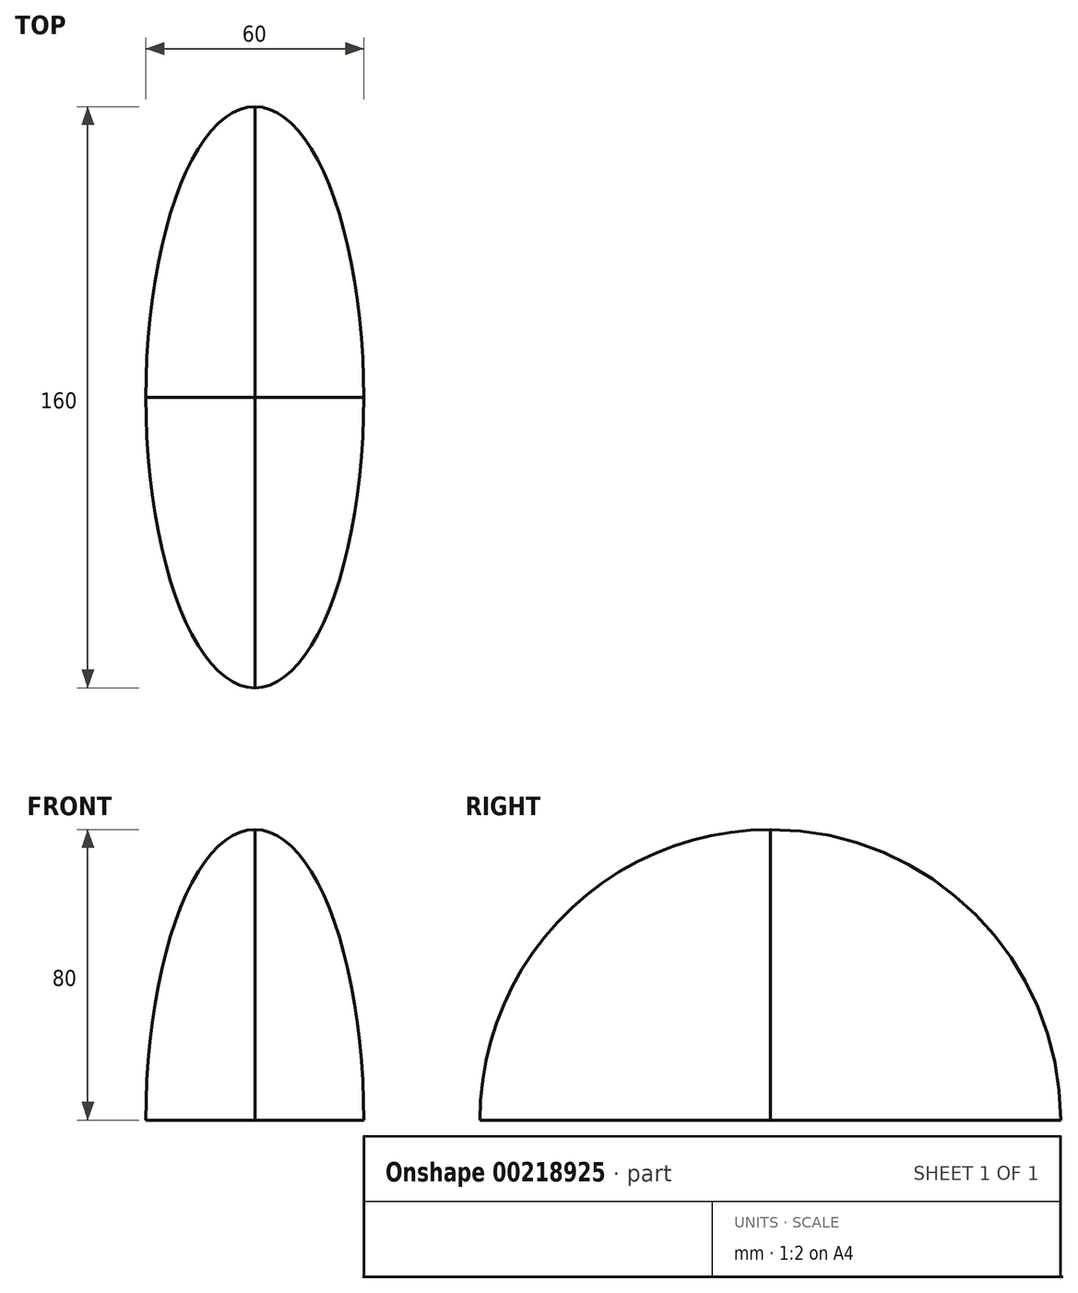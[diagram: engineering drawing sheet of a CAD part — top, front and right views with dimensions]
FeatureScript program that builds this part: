
annotation { "Feature Type Name" : "Feature", "Feature Type Description" : "" }
export const myFeature = defineFeature(function(context is Context, id is Id, definition is map)
    precondition{}
    {
        {
            var Q0;
            Q0=qCreatedBy(makeId("Top.planeOp"),FACE);
            var sketch = newSketch(context, id + "F0", { "sketchPlane" : qUnion([Q0])});
            skEllipticalArc(sketch, "E0", {});
            const initialGuessF0  = {"E0": [0, 0, 1, 0, 0.03, 0.08, 6.283185307179586, 1.5707963267948966]};
            skSetInitialGuess(sketch, initialGuessF0);
            skSolve(sketch);
        }
        {
            var Q0;
            Q0=qCreatedBy(makeId("Right.planeOp"),FACE);
            var sketch = newSketch(context, id + "F1", { "sketchPlane" : qUnion([Q0])});
            skArc(sketch, "E1", {"start": v(80, 0) * mm, "mid": v(56.57, 56.57) * mm, "end": v(0, 80) * mm});
            skLineSegment(sketch, "E2", {"start": v(0, 0) * mm, "end": v(80, 0) * mm});
            skLineSegment(sketch, "E3", {"start": v(0, 0) * mm, "end": v(0, 80) * mm});
            skSolve(sketch);
        }
        {
            var Q0;
            Q0=qCreatedBy(makeId("Front.planeOp"),FACE);
            var sketch = newSketch(context, id + "F2", { "sketchPlane" : qUnion([Q0])});
            skEllipticalArc(sketch, "E4", {});
            skLineSegment(sketch, "E5", {"start": v(0, 0) * mm, "end": v(30, 0) * mm});
            skLineSegment(sketch, "E6", {"start": v(0, 80) * mm, "end": v(0, 0) * mm});
            const initialGuessF2  = {"E4": [0, 0, 1, 0, 0.03, 0.08, 6.283185307179586, 1.5707963267948966]};
            skSetInitialGuess(sketch, initialGuessF2);
            skSolve(sketch);
        }
        {
            var Q0;
            Q0 = qSketchRegion(id + "F2", true);
            var Q1;
            Q1 = qSketchRegion(id + "F1", true);
            var Q2;
            Q2=sQuery(id+"F0.wireOp",EDGE,"E0");
            loft(context, id + "F3", {"addGuides" : true, "sheetProfilesArray" : [{ "sheetProfileEntities" : qUnion([Q0]) }, { "sheetProfileEntities" : qUnion([Q1]) }], "guidesArray" : [{ "guideEntities" : qUnion([Q2]), "guideDerivativeType" : LoftGuideDerivativeType.DEFAULT, "guideDerivativeMagnitude" : 1 }]});
        }
        {
            var Q0;
            Q0=makeQuery(id+"F3.opLoft","SWEPT_BODY",BODY,{"disambiguationData":[OSD([sQuery(id+"F0.wireOp",EDGE,"E0"),makeQuery(id+"F1.imprint","IMPRINT",FACE,{"disambiguationData":[TD([[makeQuery(id+"F1.imprint","IMPRINT",EDGE,{"derivedFrom":sQuery(id+"F1.wireOp",EDGE,"E1")}),1.0]])]}),makeQuery(id+"F2.imprint","IMPRINT",FACE,{"disambiguationData":[TD([[makeQuery(id+"F2.imprint","IMPRINT",EDGE,{"derivedFrom":sQuery(id+"F2.wireOp",EDGE,"E4")}),1.0]])]})])]});
            var Q1;
            Q1=qCreatedBy(makeId("Right.planeOp"),FACE);
            mirror(context, id + "F4", {"operationType" : NewBodyOperationType.ADD, "entities" : qUnion([Q0]), "mirrorPlane" : qUnion([Q1])});
        }
        {
            var Q0;
            Q0=makeQuery(id+"F3.opLoft","SWEPT_BODY",BODY,{"disambiguationData":[OSD([sQuery(id+"F0.wireOp",EDGE,"E0"),makeQuery(id+"F1.imprint","IMPRINT",FACE,{"disambiguationData":[TD([[makeQuery(id+"F1.imprint","IMPRINT",EDGE,{"derivedFrom":sQuery(id+"F1.wireOp",EDGE,"E1")}),1.0]])]}),makeQuery(id+"F2.imprint","IMPRINT",FACE,{"disambiguationData":[TD([[makeQuery(id+"F2.imprint","IMPRINT",EDGE,{"derivedFrom":sQuery(id+"F2.wireOp",EDGE,"E4")}),1.0]])]})])]});
            var Q1;
            Q1=qCreatedBy(makeId("Front.planeOp"),FACE);
            mirror(context, id + "F5", {"operationType" : NewBodyOperationType.ADD, "entities" : qUnion([Q0]), "mirrorPlane" : qUnion([Q1])});
        }
    });
